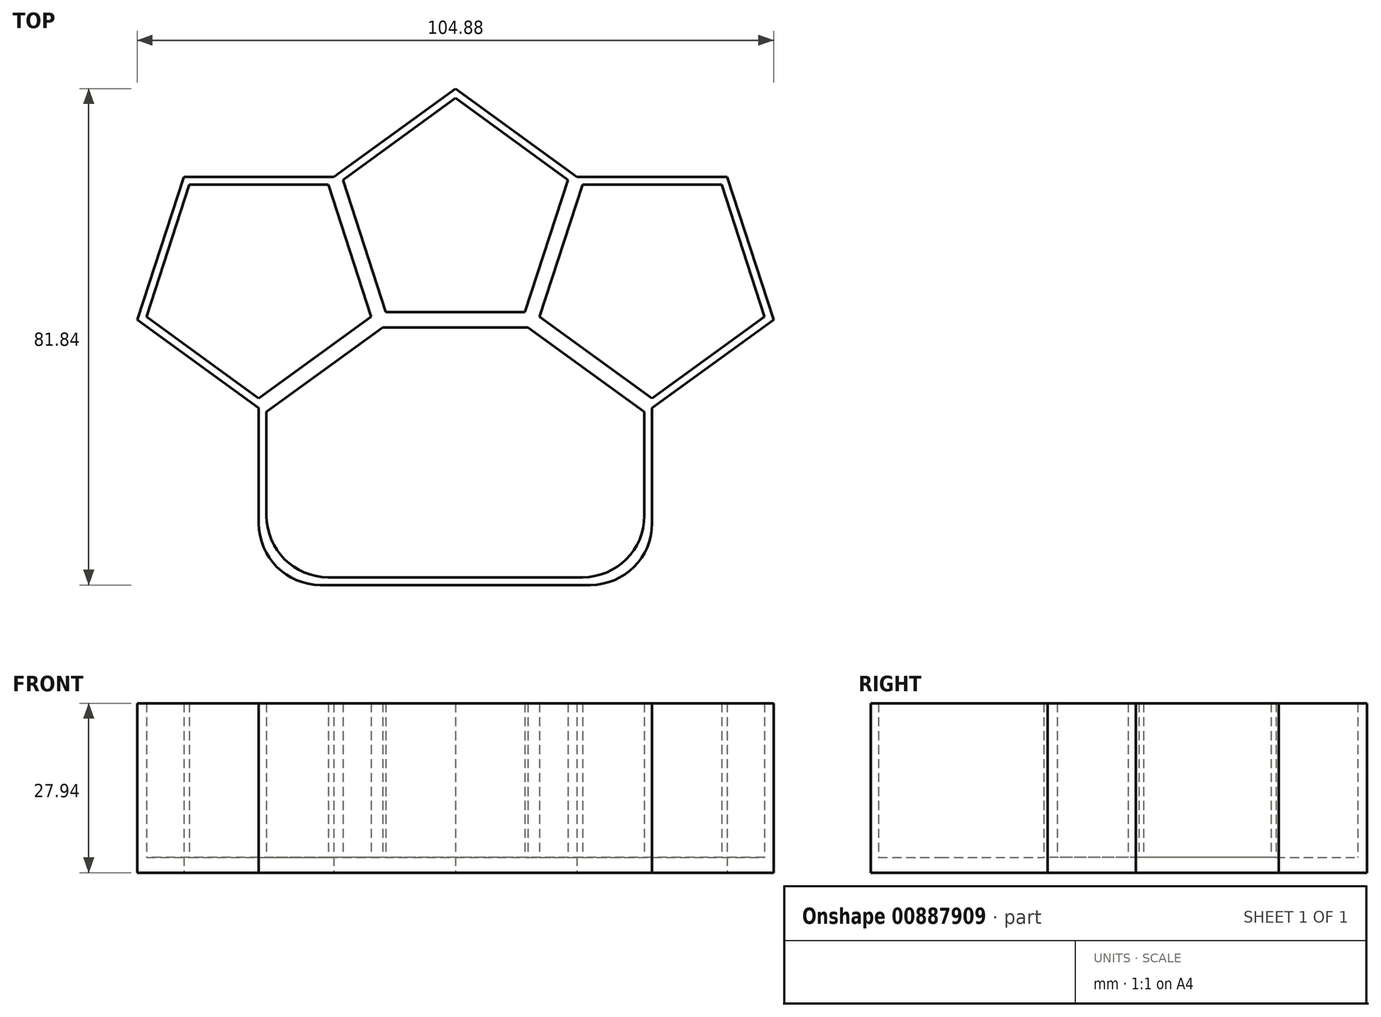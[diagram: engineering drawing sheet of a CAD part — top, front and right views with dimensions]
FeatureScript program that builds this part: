
annotation { "Feature Type Name" : "Feature", "Feature Type Description" : "" }
export const myFeature = defineFeature(function(context is Context, id is Id, definition is map)
    precondition{}
    {
        {
            var Q0;
            Q0=qCreatedBy(makeId("Top.planeOp"),FACE);
            var sketch = newSketch(context, id + "F0", { "sketchPlane" : qUnion([Q0])});
            skCircle(sketch, "E0.cCircle", {"center": v(0, 0) * mm, "radius": 17.04 * mm, "construction": true});
            skLineSegment(sketch, "E0.0", {"start": v(20.03, 6.5) * mm, "end": v(12.38, -17.04) * mm});
            skLineSegment(sketch, "E0.1", {"start": v(12.38, -17.04) * mm, "end": v(-12.38, -17.04) * mm});
            skLineSegment(sketch, "E0.2", {"start": v(-12.38, -17.04) * mm, "end": v(-20.03, 6.5) * mm});
            skLineSegment(sketch, "E0.3", {"start": v(-20.03, 6.5) * mm, "end": v(0, 21.06) * mm});
            skLineSegment(sketch, "E0.4", {"start": v(0, 21.06) * mm, "end": v(20.03, 6.5) * mm});
            skPoint(sketch, "E0.0.midPoint", {"position": v(16.2, -5.27) * mm});
            skLineSegment(sketch, "E1.0", {"start": v(0, 19.5) * mm, "end": v(18.54, 6.02) * mm});
            skLineSegment(sketch, "E1.1", {"start": v(-18.54, 6.02) * mm, "end": v(0, 19.5) * mm});
            skLineSegment(sketch, "E1.2", {"start": v(18.54, 6.02) * mm, "end": v(11.46, -15.77) * mm});
            skLineSegment(sketch, "E1.3", {"start": v(11.46, -15.77) * mm, "end": v(-11.46, -15.77) * mm});
            skLineSegment(sketch, "E1.4", {"start": v(-11.46, -15.77) * mm, "end": v(-18.54, 6.02) * mm});
            skCircle(sketch, "E2.cCircle", {"center": v(-32.4, -10.53) * mm, "radius": 17.04 * mm, "construction": true});
            skLineSegment(sketch, "E2.0", {"start": v(-12.38, -17.04) * mm, "end": v(-32.4, -31.6) * mm});
            skLineSegment(sketch, "E2.1", {"start": v(-32.4, -31.6) * mm, "end": v(-52.44, -17.04) * mm});
            skLineSegment(sketch, "E2.2", {"start": v(-52.44, -17.04) * mm, "end": v(-44.79, 6.5) * mm});
            skLineSegment(sketch, "E2.3", {"start": v(-44.79, 6.5) * mm, "end": v(-20.03, 6.5) * mm});
            skLineSegment(sketch, "E2.4", {"start": v(-20.03, 6.5) * mm, "end": v(-12.38, -17.04) * mm});
            skPoint(sketch, "E2.0.midPoint", {"position": v(-22.4, -24.32) * mm});
            skLineSegment(sketch, "E3.0", {"start": v(-20.95, 5.24) * mm, "end": v(-13.87, -16.55) * mm});
            skLineSegment(sketch, "E3.1", {"start": v(-43.87, 5.24) * mm, "end": v(-20.95, 5.24) * mm});
            skLineSegment(sketch, "E3.2", {"start": v(-13.87, -16.55) * mm, "end": v(-32.4, -30.02) * mm});
            skLineSegment(sketch, "E3.3", {"start": v(-32.4, -30.02) * mm, "end": v(-50.95, -16.55) * mm});
            skLineSegment(sketch, "E3.4", {"start": v(-50.95, -16.55) * mm, "end": v(-43.87, 5.24) * mm});
            skLineSegment(sketch, "E4.2", {"start": v(52.44, -17.04) * mm, "end": v(44.79, 6.5) * mm});
            skCircle(sketch, "E5.cCircle", {"center": v(32.4, -10.53) * mm, "radius": 17.04 * mm, "construction": true});
            skLineSegment(sketch, "E5.0", {"start": v(52.44, -17.04) * mm, "end": v(32.4, -31.6) * mm});
            skLineSegment(sketch, "E5.1", {"start": v(32.4, -31.6) * mm, "end": v(12.38, -17.04) * mm});
            skLineSegment(sketch, "E5.2", {"start": v(12.38, -17.04) * mm, "end": v(20.03, 6.5) * mm});
            skLineSegment(sketch, "E5.3", {"start": v(20.03, 6.5) * mm, "end": v(44.79, 6.5) * mm});
            skLineSegment(sketch, "E5.4", {"start": v(44.79, 6.5) * mm, "end": v(52.44, -17.04) * mm});
            skPoint(sketch, "E5.0.midPoint", {"position": v(42.42, -24.32) * mm});
            skLineSegment(sketch, "E6.0", {"start": v(43.87, 5.24) * mm, "end": v(50.95, -16.55) * mm});
            skLineSegment(sketch, "E6.1", {"start": v(20.95, 5.24) * mm, "end": v(43.87, 5.24) * mm});
            skLineSegment(sketch, "E6.2", {"start": v(50.95, -16.55) * mm, "end": v(32.4, -30.02) * mm});
            skLineSegment(sketch, "E6.3", {"start": v(32.4, -30.02) * mm, "end": v(13.87, -16.55) * mm});
            skLineSegment(sketch, "E6.4", {"start": v(13.87, -16.55) * mm, "end": v(20.95, 5.24) * mm});
            skLineSegment(sketch, "E7", {"start": v(-32.4, -31.6) * mm, "end": v(-12.38, -17.04) * mm});
            skLineSegment(sketch, "E8", {"start": v(12.38, -17.04) * mm, "end": v(32.4, -31.6) * mm});
            skLineSegment(sketch, "E9", {"start": v(32.4, -60.78) * mm, "end": v(-32.4, -60.78) * mm});
            skLineSegment(sketch, "E10", {"start": v(-32.4, -60.78) * mm, "end": v(-32.4, -31.6) * mm});
            skLineSegment(sketch, "E11", {"start": v(32.4, -60.78) * mm, "end": v(32.4, -31.6) * mm});
            skLineSegment(sketch, "E12.0", {"start": v(31.14, -59.5) * mm, "end": v(31.14, -32.24) * mm});
            skLineSegment(sketch, "E12.1", {"start": v(-31.14, -59.5) * mm, "end": v(-31.14, -32.24) * mm});
            skLineSegment(sketch, "E12.2", {"start": v(-11.97, -18.3) * mm, "end": v(-31.14, -32.24) * mm});
            skLineSegment(sketch, "E12.3", {"start": v(31.14, -59.5) * mm, "end": v(-31.14, -59.5) * mm});
            skLineSegment(sketch, "E12.4", {"start": v(11.97, -18.3) * mm, "end": v(-11.97, -18.3) * mm});
            skLineSegment(sketch, "E12.5", {"start": v(11.97, -18.3) * mm, "end": v(31.14, -32.24) * mm});
            skSolve(sketch);
        }
        {
            var Q0;
            Q0 = qSketchRegion(id + "F0", true);
            extrude(context, id + "F1", {"entities" : qUnion([Q0]), "depth" : 25.4 * mm, "offsetDistance" : 25.4 * mm});
        }
        {
            var Q0;
            Q0=qCreatedBy(makeId("Top.planeOp"),FACE);
            var sketch = newSketch(context, id + "F2", { "sketchPlane" : qUnion([Q0])});
            skCircle(sketch, "E13.cCircle", {"center": v(0, 0) * mm, "radius": 17.04 * mm, "construction": true});
            skLineSegment(sketch, "E13.3", {"start": v(-20.03, 6.5) * mm, "end": v(0, 21.06) * mm});
            skLineSegment(sketch, "E13.4", {"start": v(0, 21.06) * mm, "end": v(20.03, 6.5) * mm});
            skPoint(sketch, "E13.0.midPoint", {"position": v(16.2, -5.27) * mm});
            skLineSegment(sketch, "E14.0", {"start": v(0, 19.5) * mm, "end": v(18.54, 6.02) * mm});
            skCircle(sketch, "E15.cCircle", {"center": v(-32.4, -10.53) * mm, "radius": 17.04 * mm, "construction": true});
            skLineSegment(sketch, "E15.1", {"start": v(-32.4, -31.6) * mm, "end": v(-52.44, -17.04) * mm});
            skLineSegment(sketch, "E15.2", {"start": v(-52.44, -17.04) * mm, "end": v(-44.79, 6.5) * mm});
            skLineSegment(sketch, "E15.3", {"start": v(-44.79, 6.5) * mm, "end": v(-20.03, 6.5) * mm});
            skLineSegment(sketch, "E16.1", {"start": v(-43.87, 5.24) * mm, "end": v(-20.95, 5.24) * mm});
            skLineSegment(sketch, "E16.3", {"start": v(-32.4, -30.02) * mm, "end": v(-50.95, -16.55) * mm});
            skLineSegment(sketch, "E16.4", {"start": v(-50.95, -16.55) * mm, "end": v(-43.87, 5.24) * mm});
            skLineSegment(sketch, "E17.2", {"start": v(52.44, -17.04) * mm, "end": v(44.79, 6.5) * mm});
            skCircle(sketch, "E18.cCircle", {"center": v(32.4, -10.53) * mm, "radius": 17.04 * mm, "construction": true});
            skLineSegment(sketch, "E18.0", {"start": v(52.44, -17.04) * mm, "end": v(32.4, -31.6) * mm});
            skLineSegment(sketch, "E18.1", {"start": v(32.4, -31.6) * mm, "end": v(12.38, -17.04) * mm});
            skLineSegment(sketch, "E18.3", {"start": v(20.03, 6.5) * mm, "end": v(44.79, 6.5) * mm});
            skLineSegment(sketch, "E18.4", {"start": v(44.79, 6.5) * mm, "end": v(52.44, -17.04) * mm});
            skPoint(sketch, "E18.0.midPoint", {"position": v(42.42, -24.32) * mm});
            skLineSegment(sketch, "E19", {"start": v(32.4, -60.78) * mm, "end": v(-32.4, -60.78) * mm});
            skLineSegment(sketch, "E20", {"start": v(-32.4, -60.78) * mm, "end": v(-32.4, -31.6) * mm});
            skLineSegment(sketch, "E21", {"start": v(32.4, -60.78) * mm, "end": v(32.4, -31.6) * mm});
            skSolve(sketch);
        }
        {
            var Q0;
            Q0 = qSketchRegion(id + "F2", true);
            extrude(context, id + "F3", {"entities" : qUnion([Q0]), "operationType" : NewBodyOperationType.ADD, "oppositeDirection" : true, "depth" : 2.54 * mm, "offsetDistance" : 25.4 * mm});
        }
        {
            var Q0;
            Q0=makeQuery(id+"F3.boolean.opBoolean","MERGE",EDGE,{"derivedFrom":[makeQuery(id+"F1.opExtrude","SWEPT_EDGE",EDGE,{"disambiguationData":[OSD([sQuery(id+"F0.wireOp",EDGE,"E9"),sQuery(id+"F0.wireOp",EDGE,"E11")])]}),makeQuery(id+"F3.opExtrude","SWEPT_EDGE",EDGE,{"disambiguationData":[OSD([sQuery(id+"F2.wireOp",EDGE,"E19"),sQuery(id+"F2.wireOp",EDGE,"E21")])]})]});
            var Q1;
            Q1=makeQuery(id+"F3.boolean.opBoolean","MERGE",EDGE,{"derivedFrom":[makeQuery(id+"F1.opExtrude","SWEPT_EDGE",EDGE,{"disambiguationData":[OSD([sQuery(id+"F0.wireOp",EDGE,"E9"),sQuery(id+"F0.wireOp",EDGE,"E10")])]}),makeQuery(id+"F3.opExtrude","SWEPT_EDGE",EDGE,{"disambiguationData":[OSD([sQuery(id+"F2.wireOp",EDGE,"E19"),sQuery(id+"F2.wireOp",EDGE,"E20")])]})]});
            var Q2;
            Q2=makeQuery(id+"F1.opExtrude","SWEPT_EDGE",EDGE,{"disambiguationData":[OSD([sQuery(id+"F0.wireOp",EDGE,"E12.1"),sQuery(id+"F0.wireOp",EDGE,"E12.3")])]});
            var Q3;
            Q3=makeQuery(id+"F1.opExtrude","SWEPT_EDGE",EDGE,{"disambiguationData":[OSD([sQuery(id+"F0.wireOp",EDGE,"E12.0"),sQuery(id+"F0.wireOp",EDGE,"E12.3")])]});
            fillet(context, id + "F4", {"entities" : qUnion([Q0, Q1, Q2, Q3]), "radius" : 10.16 * mm, "tangentPropagation" : true, "allowEdgeOverflow" : false});
        }
    });
